# Revit family: NLRS_57_DUA_UN_rectangular-heater-ah_kk-LT_sacs
name_source: partatom
category: Duct Accessories
units: mm (PartAtom-declared; Revit-internal decimal feet)

## family parameters
Always vertical = Yes
Cut with Voids When Loaded = No
OmniClass Number = 23.75.10.11.17
OmniClass Title = Warm Air Heat Generators
Part Type = Breaks Into
Round Connector Dimension = Use Diameter
Shared = No
Work Plane-Based = No

## types (1)
- AH_KK heater
    Assembly Code = 57.00
    Cost = 0 $
    Description = Heater battery AH_KK - Rectangular connector - Solid Air
    IfcDescription = Heater battery AH_KK - Rectangular connector - Solid Air
    IfcExportAs = IfcHeatExchanger
    IfcExportType = Heater
    Manufacturer = Solid Air Climate Solutions
    Model = AH_KK
    NLRS_C_content_datum_uitgifte = 05-07-2022
    NLRS_C_content_provider = Solid Air Climate Solutions
    NLRS_C_content_versie = 3.19.03
    NLRS_C_description = Heater battery AH_KK - Rectangular connector - Solid Air
    SACS_Article_Data = AH-KK_Data
    Type Comments = Check flow directions!
    URL = https://solid-air.nl

## geometry (parser evidence)
native form markers: Sweep x8
no freeform markers — native parametric forms only
